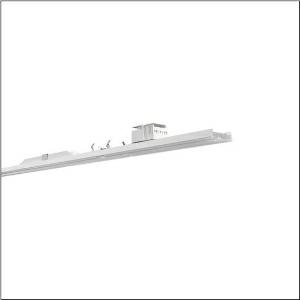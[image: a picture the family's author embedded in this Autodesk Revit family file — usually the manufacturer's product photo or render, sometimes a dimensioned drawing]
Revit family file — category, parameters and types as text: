
# Revit family: licross_r__11_recessed_mo_51tl187n48xf_f777
name_source: partatom
category: Lighting Fixtures
units: mm (PartAtom-declared; Revit-internal decimal feet)

## family parameters
Cut with Voids When Loaded = No
Host = Face
Light Source = No
Part Type = Normal
Room Calculation Point = No
Round Connector Dimension = Use Diameter
Shared = No

## types (1)
- Licross® 11 Recessed MO (1 x LED, 8150 lm, 47.6 W, 4000K)
    Apparent Load = 48 VA
    CIE Flux Codes = 83 96 99 100 100
    Color Rendering = 80
    Color Temperature = 4000K
    Default Elevation = 1800 mm
    Description = Licross® 11 Recessed MOluminaire insert, length: 1.500mm, width: 66mm, height: 67mm, LED rated luminous flux: 8.150lm, light colour: 840, control gear: ON/OFF, control gear: ECG, with plug, 3-pole, with phase selection, mains connection: 220..240V, AC, 50/60Hz, halogen-free wiring, primary optical cover: cover, of PMMA, light emission: direct distribution, protection rating (complete): IP40, insulation class (complete): insulation class I (protective earthing), certification: CE, ENEC, VDE, protection symbol: D if used in an environment without relevant dust loads with corresponding accessories, permissible ambient temperature for indoor applications: -35..+40°C, reducing of maximum allowable ambient temperature of 5°C with ceiling mounting, corresponds to IFS (International Featured Standards) requirements for safety and quality in the food industry, packaging unit: 1 piece
    Height = 58 mm
    Lamp = 1 x LED
    Lamp Light Flux = 8150 lm
    Lamp Power = 47.6 W
    Lamp count = 1
    Length = 1500 mm
    Luminous efficacy = 171 lm/W
    Manufacturer = Siteco
    ModVariant = No
    Model = 51TL187N48XF
    Mounting Place = Ceiling
    Mounting Type = Pendant
    Number of Poles = 1
    OnlyDefault = Yes
    Power Factor = 1
    Product Name = Licross® 11 Recessed MO
    Product group = luminaire insert
    ProductGroupID = 902
    Protection Class = Protection class I
    Protection Degree = IP 40
    RLX_Detail_Level = 1
    RlxData = <blob elided: 18841 chars, md5=84dac2ed>
    Socket = socket
    Standby Power = 0 W
    System Light Flux = 8150 lm
    System Power = 48 W
    Type Comments = Product without accessories
    Type Image = l_1266722.jpg
    URL = http://relux.com
    VarID = ---
    Voltage = 0 V
    Weight = 0.00 kg
    Width = 66 mm

## geometry (parser evidence)
native form markers: Blend x4, Sweep x10
no freeform markers — native parametric forms only
